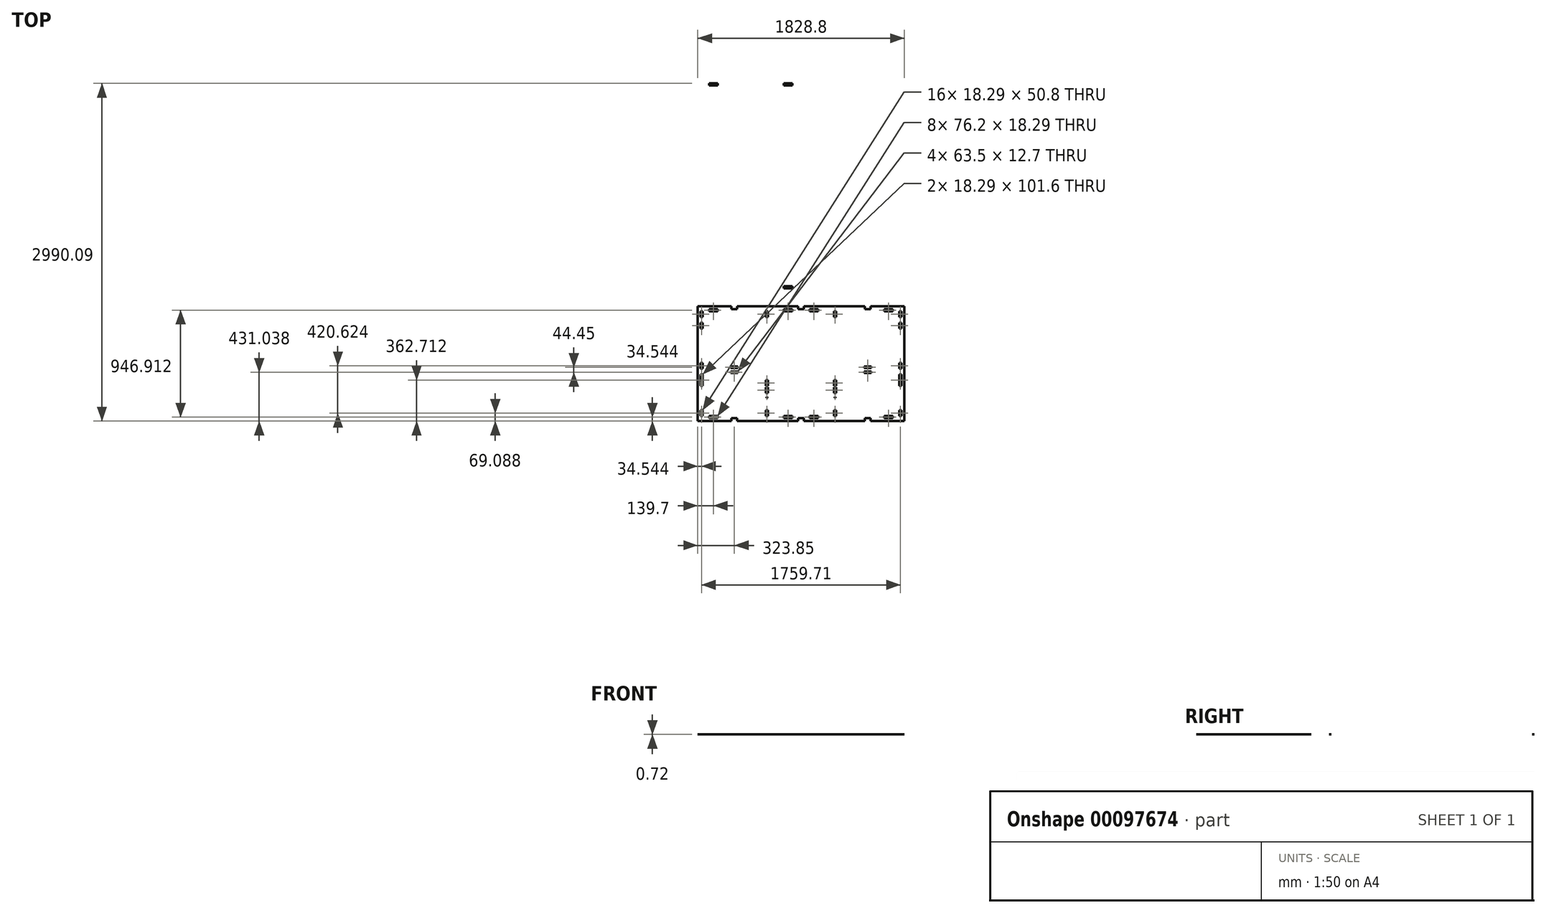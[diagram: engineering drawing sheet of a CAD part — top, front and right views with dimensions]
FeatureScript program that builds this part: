
annotation { "Feature Type Name" : "Feature", "Feature Type Description" : "" }
export const myFeature = defineFeature(function(context is Context, id is Id, definition is map)
    precondition{}
    {
        {
            assignVariable(context, id + "F0", {"name" : "ply34", "anyValue" : .72});
        }
        {
            var Q0;
            Q0=qCreatedBy(makeId("Top.planeOp"),FACE);
            var sketch = newSketch(context, id + "F1", { "sketchPlane" : qUnion([Q0])});
            skLineSegment(sketch, "E0.bottom", {"start": v(914.4, 508) * mm, "end": v(-914.4, 508) * mm});
            skLineSegment(sketch, "E0.top", {"start": v(914.4, -508) * mm, "end": v(-914.4, -508) * mm});
            skLineSegment(sketch, "E0.left", {"start": v(914.4, 508) * mm, "end": v(914.4, -508) * mm});
            skLineSegment(sketch, "E0.right", {"start": v(-914.4, 508) * mm, "end": v(-914.4, -508) * mm});
            skPoint(sketch, "E0.middle", {"position": v(0, 0) * mm});
            skLineSegment(sketch, "E1.bottom", {"start": v(889, 482.6) * mm, "end": v(-889, 482.6) * mm, "construction": true});
            skLineSegment(sketch, "E1.top", {"start": v(889, -482.6) * mm, "end": v(-889, -482.6) * mm, "construction": true});
            skLineSegment(sketch, "E1.left", {"start": v(889, 482.6) * mm, "end": v(889, -482.6) * mm, "construction": true});
            skLineSegment(sketch, "E1.right", {"start": v(-889, 482.6) * mm, "end": v(-889, -482.6) * mm, "construction": true});
            skLineSegment(sketch, "E2", {"start": v(0, 482.6) * mm, "end": v(0, -482.6) * mm, "construction": true});
            skLineSegment(sketch, "E3", {"start": v(0, 0) * mm, "end": v(-889, 0) * mm, "construction": true});
            skLineSegment(sketch, "E4", {"start": v(-444.5, 482.6) * mm, "end": v(-444.5, -482.6) * mm, "construction": true});
            skPoint(sketch, "E4.startSnap0", {"position": v(-444.5, 0) * mm});
            skLineSegment(sketch, "E5.bottom", {"start": v(-812.8, 482.6) * mm, "end": v(-736.6, 482.6) * mm});
            skLineSegment(sketch, "E5.top", {"start": v(-812.8, 464.31) * mm, "end": v(-736.6, 464.31) * mm});
            skLineSegment(sketch, "E5.left", {"start": v(-812.8, 482.6) * mm, "end": v(-812.8, 464.31) * mm});
            skLineSegment(sketch, "E5.right", {"start": v(-736.6, 482.6) * mm, "end": v(-736.6, 464.31) * mm});
            skLineSegment(sketch, "E6.MirrorCS", {"start": v(-76.2, 482.6) * mm, "end": v(-152.4, 482.6) * mm});
            skLineSegment(sketch, "E7.MirrorCS", {"start": v(-76.2, 464.31) * mm, "end": v(-152.4, 464.31) * mm});
            skLineSegment(sketch, "E8.MirrorCS", {"start": v(-152.4, 482.6) * mm, "end": v(-152.4, 464.31) * mm});
            skLineSegment(sketch, "E9.MirrorCS", {"start": v(-76.2, 482.6) * mm, "end": v(-76.2, 464.31) * mm});
            skLineSegment(sketch, "E10.MirrorCS", {"start": v(76.2, 482.6) * mm, "end": v(76.2, 464.31) * mm});
            skLineSegment(sketch, "E11.MirrorCS", {"start": v(736.6, 482.6) * mm, "end": v(736.6, 464.31) * mm});
            skLineSegment(sketch, "E12.MirrorCS", {"start": v(152.4, 482.6) * mm, "end": v(152.4, 464.31) * mm});
            skLineSegment(sketch, "E13.MirrorCS", {"start": v(812.8, 482.6) * mm, "end": v(812.8, 464.31) * mm});
            skLineSegment(sketch, "E14.MirrorCS", {"start": v(812.8, 482.6) * mm, "end": v(736.6, 482.6) * mm});
            skLineSegment(sketch, "E15.MirrorCS", {"start": v(76.2, 482.6) * mm, "end": v(152.4, 482.6) * mm});
            skLineSegment(sketch, "E16.MirrorCS", {"start": v(812.8, 464.31) * mm, "end": v(736.6, 464.31) * mm});
            skLineSegment(sketch, "E17.MirrorCS", {"start": v(76.2, 464.31) * mm, "end": v(152.4, 464.31) * mm});
            skLineSegment(sketch, "E18.MirrorCS", {"start": v(812.8, -482.6) * mm, "end": v(812.8, -464.31) * mm});
            skLineSegment(sketch, "E19.MirrorCS", {"start": v(-76.2, -482.6) * mm, "end": v(-76.2, -464.31) * mm});
            skLineSegment(sketch, "E20.MirrorCS", {"start": v(736.6, -482.6) * mm, "end": v(736.6, -464.31) * mm});
            skLineSegment(sketch, "E21.MirrorCS", {"start": v(-152.4, -482.6) * mm, "end": v(-152.4, -464.31) * mm});
            skLineSegment(sketch, "E22.MirrorCS", {"start": v(152.4, -482.6) * mm, "end": v(152.4, -464.31) * mm});
            skLineSegment(sketch, "E23.MirrorCS", {"start": v(-812.8, -482.6) * mm, "end": v(-812.8, -464.31) * mm});
            skLineSegment(sketch, "E24.MirrorCS", {"start": v(76.2, -482.6) * mm, "end": v(76.2, -464.31) * mm});
            skLineSegment(sketch, "E25.MirrorCS", {"start": v(-736.6, -482.6) * mm, "end": v(-736.6, -464.31) * mm});
            skLineSegment(sketch, "E26.MirrorCS", {"start": v(76.2, -482.6) * mm, "end": v(152.4, -482.6) * mm});
            skLineSegment(sketch, "E27.MirrorCS", {"start": v(812.8, -464.31) * mm, "end": v(736.6, -464.31) * mm});
            skLineSegment(sketch, "E28.MirrorCS", {"start": v(812.8, -482.6) * mm, "end": v(736.6, -482.6) * mm});
            skLineSegment(sketch, "E29.MirrorCS", {"start": v(-76.2, -464.31) * mm, "end": v(-152.4, -464.31) * mm});
            skLineSegment(sketch, "E30.MirrorCS", {"start": v(-76.2, -482.6) * mm, "end": v(-152.4, -482.6) * mm});
            skLineSegment(sketch, "E31.MirrorCS", {"start": v(76.2, -464.31) * mm, "end": v(152.4, -464.31) * mm});
            skLineSegment(sketch, "E32.MirrorCS", {"start": v(-812.8, -464.31) * mm, "end": v(-736.6, -464.31) * mm});
            skLineSegment(sketch, "E33.MirrorCS", {"start": v(-812.8, -482.6) * mm, "end": v(-736.6, -482.6) * mm});
            skLineSegment(sketch, "E34.bottom", {"start": v(292.1, 464.31) * mm, "end": v(310.39, 464.31) * mm});
            skLineSegment(sketch, "E34.top", {"start": v(292.1, 413.51) * mm, "end": v(310.39, 413.51) * mm});
            skLineSegment(sketch, "E34.left", {"start": v(292.1, 464.31) * mm, "end": v(292.1, 413.51) * mm});
            skLineSegment(sketch, "E34.right", {"start": v(310.39, 464.31) * mm, "end": v(310.39, 413.51) * mm});
            skLineSegment(sketch, "E35.bottom", {"start": v(292.1, -145.29) * mm, "end": v(310.39, -145.29) * mm});
            skLineSegment(sketch, "E35.top", {"start": v(292.1, -196.09) * mm, "end": v(310.39, -196.09) * mm});
            skLineSegment(sketch, "E35.left", {"start": v(292.1, -145.29) * mm, "end": v(292.1, -196.09) * mm});
            skLineSegment(sketch, "E35.right", {"start": v(310.39, -145.29) * mm, "end": v(310.39, -196.09) * mm});
            skLineSegment(sketch, "E36.MirrorCS", {"start": v(-292.1, -196.09) * mm, "end": v(-310.39, -196.09) * mm});
            skLineSegment(sketch, "E37.MirrorCS", {"start": v(-292.1, -145.29) * mm, "end": v(-310.39, -145.29) * mm});
            skLineSegment(sketch, "E38.MirrorCS", {"start": v(-292.1, 413.51) * mm, "end": v(-310.39, 413.51) * mm});
            skLineSegment(sketch, "E39.MirrorCS", {"start": v(-292.1, 464.31) * mm, "end": v(-310.39, 464.31) * mm});
            skLineSegment(sketch, "E40.MirrorCS", {"start": v(-292.1, -145.29) * mm, "end": v(-292.1, -196.09) * mm});
            skLineSegment(sketch, "E41.MirrorCS", {"start": v(-310.39, 464.31) * mm, "end": v(-310.39, 413.51) * mm});
            skLineSegment(sketch, "E42.MirrorCS", {"start": v(-310.39, -145.29) * mm, "end": v(-310.39, -196.09) * mm});
            skLineSegment(sketch, "E43.MirrorCS", {"start": v(-292.1, 464.31) * mm, "end": v(-292.1, 413.51) * mm});
            skLineSegment(sketch, "E44.bottom", {"start": v(-889, 685.8) * mm, "end": v(0, 685.8) * mm});
            skLineSegment(sketch, "E44.top", {"start": v(-889, 2463.8) * mm, "end": v(0, 2463.8) * mm});
            skLineSegment(sketch, "E44.left", {"start": v(-889, 685.8) * mm, "end": v(-889, 2463.8) * mm});
            skLineSegment(sketch, "E44.right", {"start": v(0, 685.8) * mm, "end": v(0, 2463.8) * mm});
            skLineSegment(sketch, "E45.bottom", {"start": v(-812.8, 685.8) * mm, "end": v(-736.6, 685.8) * mm});
            skLineSegment(sketch, "E45.top", {"start": v(-812.8, 667.51) * mm, "end": v(-736.6, 667.51) * mm});
            skLineSegment(sketch, "E45.left", {"start": v(-812.8, 685.8) * mm, "end": v(-812.8, 667.51) * mm});
            skLineSegment(sketch, "E45.right", {"start": v(-736.6, 685.8) * mm, "end": v(-736.6, 667.51) * mm});
            skLineSegment(sketch, "E46", {"start": v(-444.5, 685.8) * mm, "end": v(-444.5, 2463.8) * mm, "construction": true});
            skLineSegment(sketch, "E47", {"start": v(0, 1574.8) * mm, "end": v(-889, 1574.8) * mm, "construction": true});
            skLineSegment(sketch, "E48.MirrorCS", {"start": v(-76.2, 667.51) * mm, "end": v(-152.4, 667.51) * mm});
            skLineSegment(sketch, "E49.MirrorCS", {"start": v(-76.2, 685.8) * mm, "end": v(-152.4, 685.8) * mm});
            skLineSegment(sketch, "E50.MirrorCS", {"start": v(-152.4, 685.8) * mm, "end": v(-152.4, 667.51) * mm});
            skLineSegment(sketch, "E51.MirrorCS", {"start": v(-76.2, 685.8) * mm, "end": v(-76.2, 667.51) * mm});
            skLineSegment(sketch, "E52.MirrorCS", {"start": v(-812.8, 2482.09) * mm, "end": v(-736.6, 2482.09) * mm});
            skLineSegment(sketch, "E53.MirrorCS", {"start": v(-812.8, 2463.8) * mm, "end": v(-736.6, 2463.8) * mm});
            skLineSegment(sketch, "E54.MirrorCS", {"start": v(-812.8, 2463.8) * mm, "end": v(-812.8, 2482.09) * mm});
            skLineSegment(sketch, "E55.MirrorCS", {"start": v(-736.6, 2463.8) * mm, "end": v(-736.6, 2482.09) * mm});
            skLineSegment(sketch, "E56.MirrorCS", {"start": v(-152.4, 2463.8) * mm, "end": v(-152.4, 2482.09) * mm});
            skLineSegment(sketch, "E57.MirrorCS", {"start": v(-76.2, 2463.8) * mm, "end": v(-76.2, 2482.09) * mm});
            skLineSegment(sketch, "E58.MirrorCS", {"start": v(-76.2, 2482.09) * mm, "end": v(-152.4, 2482.09) * mm});
            skLineSegment(sketch, "E59.MirrorCS", {"start": v(-76.2, 2463.8) * mm, "end": v(-152.4, 2463.8) * mm});
            skLineSegment(sketch, "E60.0", {"start": v(870.71, 464.31) * mm, "end": v(-870.71, 464.31) * mm, "construction": true});
            skLineSegment(sketch, "E60.1", {"start": v(870.71, 464.31) * mm, "end": v(870.71, -464.31) * mm, "construction": true});
            skLineSegment(sketch, "E60.2", {"start": v(870.71, -464.31) * mm, "end": v(-870.71, -464.31) * mm, "construction": true});
            skLineSegment(sketch, "E60.3", {"start": v(-870.71, 464.31) * mm, "end": v(-870.71, -464.31) * mm, "construction": true});
            skLineSegment(sketch, "E61.bottom", {"start": v(-310.39, 464.31) * mm, "end": v(-292.1, 464.31) * mm, "construction": true});
            skLineSegment(sketch, "E61.top", {"start": v(-310.39, -196.09) * mm, "end": v(-292.1, -196.09) * mm, "construction": true});
            skLineSegment(sketch, "E61.left", {"start": v(-310.39, 464.31) * mm, "end": v(-310.39, -196.09) * mm, "construction": true});
            skLineSegment(sketch, "E61.right", {"start": v(-292.1, 464.31) * mm, "end": v(-292.1, -196.09) * mm, "construction": true});
            skLineSegment(sketch, "E62.bottom", {"start": v(292.1, 464.31) * mm, "end": v(310.39, 464.31) * mm, "construction": true});
            skLineSegment(sketch, "E62.top", {"start": v(292.1, -196.09) * mm, "end": v(310.39, -196.09) * mm, "construction": true});
            skLineSegment(sketch, "E62.left", {"start": v(292.1, 464.31) * mm, "end": v(292.1, -196.09) * mm, "construction": true});
            skLineSegment(sketch, "E62.right", {"start": v(310.39, 464.31) * mm, "end": v(310.39, -196.09) * mm, "construction": true});
            skLineSegment(sketch, "E63.bottom", {"start": v(889, 464.31) * mm, "end": v(870.71, 464.31) * mm});
            skLineSegment(sketch, "E63.top", {"start": v(889, 413.51) * mm, "end": v(870.71, 413.51) * mm});
            skLineSegment(sketch, "E63.left", {"start": v(889, 464.31) * mm, "end": v(889, 413.51) * mm});
            skLineSegment(sketch, "E63.right", {"start": v(870.71, 464.31) * mm, "end": v(870.71, 413.51) * mm});
            skLineSegment(sketch, "E64.bottom", {"start": v(889, -94.49) * mm, "end": v(870.71, -94.49) * mm});
            skLineSegment(sketch, "E64.top", {"start": v(889, -145.29) * mm, "end": v(870.71, -145.29) * mm});
            skLineSegment(sketch, "E64.left", {"start": v(889, -94.49) * mm, "end": v(889, -145.29) * mm});
            skLineSegment(sketch, "E64.right", {"start": v(870.71, -94.49) * mm, "end": v(870.71, -145.29) * mm});
            skLineSegment(sketch, "E65.MirrorCS", {"start": v(-889, 464.31) * mm, "end": v(-870.71, 464.31) * mm});
            skLineSegment(sketch, "E66.MirrorCS", {"start": v(-889, -145.29) * mm, "end": v(-870.71, -145.29) * mm});
            skLineSegment(sketch, "E67.MirrorCS", {"start": v(-889, -94.49) * mm, "end": v(-870.71, -94.49) * mm});
            skLineSegment(sketch, "E68.MirrorCS", {"start": v(-889, 413.51) * mm, "end": v(-870.71, 413.51) * mm});
            skLineSegment(sketch, "E69.MirrorCS", {"start": v(-870.71, -94.49) * mm, "end": v(-870.71, -145.29) * mm});
            skLineSegment(sketch, "E70.MirrorCS", {"start": v(-889, -94.49) * mm, "end": v(-889, -145.29) * mm});
            skLineSegment(sketch, "E71.MirrorCS", {"start": v(-870.71, 464.31) * mm, "end": v(-870.71, 413.51) * mm});
            skLineSegment(sketch, "E72.MirrorCS", {"start": v(-889, 464.31) * mm, "end": v(-889, 413.51) * mm});
            skLineSegment(sketch, "E73", {"start": v(-50.8, 2463.8) * mm, "end": v(-50.8, 685.8) * mm, "construction": true});
            skLineSegment(sketch, "E74.bottom", {"start": v(889, 7.11) * mm, "end": v(870.71, 7.11) * mm});
            skLineSegment(sketch, "E74.top", {"start": v(889, -43.69) * mm, "end": v(870.71, -43.69) * mm});
            skLineSegment(sketch, "E74.left", {"start": v(889, 7.11) * mm, "end": v(889, -43.69) * mm});
            skLineSegment(sketch, "E74.right", {"start": v(870.71, 7.11) * mm, "end": v(870.71, -43.69) * mm});
            skLineSegment(sketch, "E75.MirrorCS", {"start": v(-870.71, 7.11) * mm, "end": v(-870.71, -43.69) * mm});
            skLineSegment(sketch, "E76.MirrorCS", {"start": v(-889, 7.11) * mm, "end": v(-889, -43.69) * mm});
            skLineSegment(sketch, "E77.MirrorCS", {"start": v(-889, -43.69) * mm, "end": v(-870.71, -43.69) * mm});
            skLineSegment(sketch, "E78.MirrorCS", {"start": v(-889, 7.11) * mm, "end": v(-870.71, 7.11) * mm});
            skLineSegment(sketch, "E79.MirrorCS", {"start": v(-838.2, 2463.8) * mm, "end": v(-838.2, 685.8) * mm, "construction": true});
            skLineSegment(sketch, "E80.bottom", {"start": v(-50.8, 1676.4) * mm, "end": v(-69.09, 1676.4) * mm});
            skLineSegment(sketch, "E80.top", {"start": v(-50.8, 1473.2) * mm, "end": v(-69.09, 1473.2) * mm});
            skLineSegment(sketch, "E80.left", {"start": v(-50.8, 1676.4) * mm, "end": v(-50.8, 1473.2) * mm});
            skLineSegment(sketch, "E80.right", {"start": v(-69.09, 1676.4) * mm, "end": v(-69.09, 1473.2) * mm});
            skPoint(sketch, "E80.middle", {"position": v(-59.94, 1574.8) * mm});
            skLineSegment(sketch, "E81.bottom", {"start": v(-838.2, 685.8) * mm, "end": v(-819.91, 685.8) * mm});
            skLineSegment(sketch, "E81.top", {"start": v(-838.2, 698.5) * mm, "end": v(-819.91, 698.5) * mm});
            skLineSegment(sketch, "E81.left", {"start": v(-838.2, 685.8) * mm, "end": v(-838.2, 698.5) * mm});
            skLineSegment(sketch, "E81.right", {"start": v(-819.91, 685.8) * mm, "end": v(-819.91, 698.5) * mm});
            skLineSegment(sketch, "E82.MirrorCS", {"start": v(-69.09, 685.8) * mm, "end": v(-69.09, 698.5) * mm});
            skLineSegment(sketch, "E83.MirrorCS", {"start": v(-50.8, 685.8) * mm, "end": v(-50.8, 698.5) * mm});
            skLineSegment(sketch, "E84.MirrorCS", {"start": v(-50.8, 685.8) * mm, "end": v(-69.09, 685.8) * mm});
            skLineSegment(sketch, "E85.MirrorCS", {"start": v(-50.8, 698.5) * mm, "end": v(-69.09, 698.5) * mm});
            skLineSegment(sketch, "E86.MirrorCS", {"start": v(-69.09, 2463.8) * mm, "end": v(-69.09, 2451.1) * mm});
            skLineSegment(sketch, "E87.MirrorCS", {"start": v(-50.8, 2463.8) * mm, "end": v(-50.8, 2451.1) * mm});
            skLineSegment(sketch, "E88.MirrorCS", {"start": v(-50.8, 2463.8) * mm, "end": v(-69.09, 2463.8) * mm});
            skLineSegment(sketch, "E89.MirrorCS", {"start": v(-50.8, 2451.1) * mm, "end": v(-69.09, 2451.1) * mm});
            skLineSegment(sketch, "E90.MirrorCS", {"start": v(-838.2, 2463.8) * mm, "end": v(-819.91, 2463.8) * mm});
            skLineSegment(sketch, "E91.MirrorCS", {"start": v(-838.2, 2451.1) * mm, "end": v(-819.91, 2451.1) * mm});
            skLineSegment(sketch, "E92.MirrorCS", {"start": v(-819.91, 2463.8) * mm, "end": v(-819.91, 2451.1) * mm});
            skLineSegment(sketch, "E93.MirrorCS", {"start": v(-838.2, 2463.8) * mm, "end": v(-838.2, 2451.1) * mm});
            skLineSegment(sketch, "E94", {"start": v(-889, 2270.7) * mm, "end": v(0, 2270.7) * mm, "construction": true});
            skLineSegment(sketch, "E95.bottom", {"start": v(-50.8, 2359.6) * mm, "end": v(-69.09, 2359.6) * mm});
            skLineSegment(sketch, "E95.top", {"start": v(-50.8, 2181.8) * mm, "end": v(-69.09, 2181.8) * mm});
            skLineSegment(sketch, "E95.left", {"start": v(-50.8, 2359.6) * mm, "end": v(-50.8, 2181.8) * mm});
            skLineSegment(sketch, "E95.right", {"start": v(-69.09, 2359.6) * mm, "end": v(-69.09, 2181.8) * mm});
            skPoint(sketch, "E95.middle", {"position": v(-59.94, 2270.7) * mm});
            skLineSegment(sketch, "E96.MirrorCS", {"start": v(-838.2, 2181.8) * mm, "end": v(-819.91, 2181.8) * mm});
            skLineSegment(sketch, "E97.MirrorCS", {"start": v(-838.2, 2359.6) * mm, "end": v(-819.91, 2359.6) * mm});
            skLineSegment(sketch, "E98.MirrorCS", {"start": v(-819.91, 2359.6) * mm, "end": v(-819.91, 2181.8) * mm});
            skLineSegment(sketch, "E99.MirrorCS", {"start": v(-838.2, 2359.6) * mm, "end": v(-838.2, 2181.8) * mm});
            skPoint(sketch, "E100.MirrorP", {"position": v(-829.06, 2270.7) * mm});
            skLineSegment(sketch, "E101.MirrorCS", {"start": v(-50.8, 790) * mm, "end": v(-69.09, 790) * mm});
            skLineSegment(sketch, "E102.MirrorCS", {"start": v(-838.2, 967.8) * mm, "end": v(-819.91, 967.8) * mm});
            skLineSegment(sketch, "E103.MirrorCS", {"start": v(-838.2, 790) * mm, "end": v(-819.91, 790) * mm});
            skLineSegment(sketch, "E104.MirrorCS", {"start": v(-50.8, 967.8) * mm, "end": v(-69.09, 967.8) * mm});
            skLineSegment(sketch, "E105.MirrorCS", {"start": v(-50.8, 790) * mm, "end": v(-50.8, 967.8) * mm});
            skLineSegment(sketch, "E106.MirrorCS", {"start": v(-69.09, 790) * mm, "end": v(-69.09, 967.8) * mm});
            skLineSegment(sketch, "E107.MirrorCS", {"start": v(-819.91, 790) * mm, "end": v(-819.91, 967.8) * mm});
            skLineSegment(sketch, "E108.MirrorCS", {"start": v(-838.2, 790) * mm, "end": v(-838.2, 967.8) * mm});
            skPoint(sketch, "E109.MirrorP", {"position": v(-59.94, 878.9) * mm});
            skPoint(sketch, "E110.MirrorP", {"position": v(-829.06, 878.9) * mm});
            skLineSegment(sketch, "E111.MirrorCS", {"start": v(-838.2, 1473.2) * mm, "end": v(-819.91, 1473.2) * mm});
            skLineSegment(sketch, "E112.MirrorCS", {"start": v(-838.2, 1676.4) * mm, "end": v(-819.91, 1676.4) * mm});
            skPoint(sketch, "E113.MirrorP", {"position": v(-829.06, 1574.8) * mm});
            skLineSegment(sketch, "E114.MirrorCS", {"start": v(-819.91, 1676.4) * mm, "end": v(-819.91, 1473.2) * mm});
            skLineSegment(sketch, "E115.MirrorCS", {"start": v(-838.2, 1676.4) * mm, "end": v(-838.2, 1473.2) * mm});
            skLineSegment(sketch, "E116", {"start": v(-444.5, 1574.8) * mm, "end": v(-69.09, 1574.8) * mm, "construction": true});
            skLineSegment(sketch, "E117.bottom", {"start": v(870.71, -464.31) * mm, "end": v(889, -464.31) * mm});
            skLineSegment(sketch, "E117.top", {"start": v(870.71, -413.51) * mm, "end": v(889, -413.51) * mm});
            skLineSegment(sketch, "E117.left", {"start": v(870.71, -464.31) * mm, "end": v(870.71, -413.51) * mm});
            skLineSegment(sketch, "E117.right", {"start": v(889, -464.31) * mm, "end": v(889, -413.51) * mm});
            skLineSegment(sketch, "E118.bottom", {"start": v(870.71, -145.29) * mm, "end": v(889, -145.29) * mm});
            skLineSegment(sketch, "E118.top", {"start": v(870.71, -196.09) * mm, "end": v(889, -196.09) * mm});
            skLineSegment(sketch, "E118.left", {"start": v(870.71, -145.29) * mm, "end": v(870.71, -196.09) * mm});
            skLineSegment(sketch, "E118.right", {"start": v(889, -145.29) * mm, "end": v(889, -196.09) * mm});
            skLineSegment(sketch, "E119.MirrorCS", {"start": v(-889, -145.29) * mm, "end": v(-889, -196.09) * mm});
            skLineSegment(sketch, "E120.MirrorCS", {"start": v(-870.71, -145.29) * mm, "end": v(-870.71, -196.09) * mm});
            skLineSegment(sketch, "E121.MirrorCS", {"start": v(-870.71, -196.09) * mm, "end": v(-889, -196.09) * mm});
            skLineSegment(sketch, "E122.MirrorCS", {"start": v(-870.71, -464.31) * mm, "end": v(-889, -464.31) * mm});
            skLineSegment(sketch, "E123.MirrorCS", {"start": v(-889, -464.31) * mm, "end": v(-889, -413.51) * mm});
            skLineSegment(sketch, "E124.MirrorCS", {"start": v(-870.71, -464.31) * mm, "end": v(-870.71, -413.51) * mm});
            skLineSegment(sketch, "E125.MirrorCS", {"start": v(-870.71, -413.51) * mm, "end": v(-889, -413.51) * mm});
            skLineSegment(sketch, "E126.bottom", {"start": v(-889, 879.28) * mm, "end": v(-870.71, 879.28) * mm});
            skLineSegment(sketch, "E126.top", {"start": v(-889, 764.98) * mm, "end": v(-870.71, 764.98) * mm});
            skLineSegment(sketch, "E126.left", {"start": v(-889, 879.28) * mm, "end": v(-889, 764.98) * mm});
            skLineSegment(sketch, "E126.right", {"start": v(-870.71, 879.28) * mm, "end": v(-870.71, 764.98) * mm});
            skPoint(sketch, "E126.middle", {"position": v(-879.86, 822.13) * mm});
            skLineSegment(sketch, "E127.bottom", {"start": v(-889, 1428.75) * mm, "end": v(-870.71, 1428.75) * mm});
            skLineSegment(sketch, "E127.top", {"start": v(-889, 1543.05) * mm, "end": v(-870.71, 1543.05) * mm});
            skLineSegment(sketch, "E127.left", {"start": v(-889, 1428.75) * mm, "end": v(-889, 1543.05) * mm});
            skLineSegment(sketch, "E127.right", {"start": v(-870.71, 1428.75) * mm, "end": v(-870.71, 1543.05) * mm});
            skPoint(sketch, "E127.middle", {"position": v(-879.86, 1485.9) * mm});
            skLineSegment(sketch, "E128", {"start": v(-879.86, 822.13) * mm, "end": v(-879.86, 685.8) * mm, "construction": true});
            skLineSegment(sketch, "E129", {"start": v(-879.86, 1485.9) * mm, "end": v(-879.86, 685.8) * mm, "construction": true});
            skLineSegment(sketch, "E130.MirrorCS", {"start": v(0, 879.28) * mm, "end": v(-18.29, 879.28) * mm});
            skLineSegment(sketch, "E131.MirrorCS", {"start": v(0, 879.28) * mm, "end": v(0, 764.98) * mm});
            skLineSegment(sketch, "E132.MirrorCS", {"start": v(-18.29, 1428.75) * mm, "end": v(-18.29, 1543.05) * mm});
            skPoint(sketch, "E133.MirrorP", {"position": v(-9.14, 1485.9) * mm});
            skLineSegment(sketch, "E134.MirrorCS", {"start": v(0, 1428.75) * mm, "end": v(0, 1543.05) * mm});
            skPoint(sketch, "E135.MirrorP", {"position": v(-9.14, 822.13) * mm});
            skLineSegment(sketch, "E136.MirrorCS", {"start": v(0, 1543.05) * mm, "end": v(-18.29, 1543.05) * mm});
            skLineSegment(sketch, "E137.MirrorCS", {"start": v(0, 764.98) * mm, "end": v(-18.29, 764.98) * mm});
            skLineSegment(sketch, "E138.MirrorCS", {"start": v(0, 1428.75) * mm, "end": v(-18.29, 1428.75) * mm});
            skLineSegment(sketch, "E139.MirrorCS", {"start": v(-18.29, 879.28) * mm, "end": v(-18.29, 764.98) * mm});
            skLineSegment(sketch, "E140.MirrorCS", {"start": v(-889, 2270.32) * mm, "end": v(-870.71, 2270.32) * mm});
            skLineSegment(sketch, "E141.MirrorCS", {"start": v(-889, 2384.62) * mm, "end": v(-870.71, 2384.62) * mm});
            skLineSegment(sketch, "E142.MirrorCS", {"start": v(-889, 2270.32) * mm, "end": v(-889, 2384.62) * mm});
            skLineSegment(sketch, "E143.MirrorCS", {"start": v(-870.71, 2270.32) * mm, "end": v(-870.71, 2384.62) * mm});
            skLineSegment(sketch, "E144.MirrorCS", {"start": v(-889, 1720.85) * mm, "end": v(-870.71, 1720.85) * mm});
            skLineSegment(sketch, "E145.MirrorCS", {"start": v(-889, 1606.55) * mm, "end": v(-870.71, 1606.55) * mm});
            skPoint(sketch, "E146.MirrorP", {"position": v(-879.86, 2327.47) * mm});
            skLineSegment(sketch, "E147.MirrorCS", {"start": v(-889, 1720.85) * mm, "end": v(-889, 1606.55) * mm});
            skPoint(sketch, "E148.MirrorP", {"position": v(-879.86, 1663.7) * mm});
            skLineSegment(sketch, "E149.MirrorCS", {"start": v(-870.71, 1720.85) * mm, "end": v(-870.71, 1606.55) * mm});
            skLineSegment(sketch, "E150.MirrorCS", {"start": v(0, 1720.85) * mm, "end": v(-18.29, 1720.85) * mm});
            skLineSegment(sketch, "E151.MirrorCS", {"start": v(0, 2384.62) * mm, "end": v(-18.29, 2384.62) * mm});
            skLineSegment(sketch, "E152.MirrorCS", {"start": v(0, 2270.32) * mm, "end": v(-18.29, 2270.32) * mm});
            skLineSegment(sketch, "E153.MirrorCS", {"start": v(0, 1606.55) * mm, "end": v(-18.29, 1606.55) * mm});
            skLineSegment(sketch, "E154.MirrorCS", {"start": v(0, 1720.85) * mm, "end": v(0, 1606.55) * mm});
            skLineSegment(sketch, "E155.MirrorCS", {"start": v(-18.29, 1720.85) * mm, "end": v(-18.29, 1606.55) * mm});
            skLineSegment(sketch, "E156.MirrorCS", {"start": v(-18.29, 2270.32) * mm, "end": v(-18.29, 2384.62) * mm});
            skLineSegment(sketch, "E157.MirrorCS", {"start": v(0, 2270.32) * mm, "end": v(0, 2384.62) * mm});
            skPoint(sketch, "E158.MirrorP", {"position": v(-9.14, 2327.47) * mm});
            skPoint(sketch, "E159.MirrorP", {"position": v(-9.14, 1663.7) * mm});
            skLineSegment(sketch, "E160.0", {"start": v(-889, 692.15) * mm, "end": v(0, 692.15) * mm, "construction": true});
            skLineSegment(sketch, "E161.bottom", {"start": v(-292.1, 1098.55) * mm, "end": v(-310.39, 1098.55) * mm});
            skLineSegment(sketch, "E161.top", {"start": v(-292.1, 1212.85) * mm, "end": v(-310.39, 1212.85) * mm});
            skLineSegment(sketch, "E161.left", {"start": v(-292.1, 1098.55) * mm, "end": v(-292.1, 1212.85) * mm});
            skLineSegment(sketch, "E161.right", {"start": v(-310.39, 1098.55) * mm, "end": v(-310.39, 1212.85) * mm});
            skPoint(sketch, "E161.middle", {"position": v(-301.24, 1155.7) * mm});
            skPoint(sketch, "E161.middle.positionSnap0", {"position": v(-301.24, 464.31) * mm});
            skPoint(sketch, "E161.centerSnap0", {"position": v(-301.24, 464.31) * mm});
            skLineSegment(sketch, "E162.MirrorCS", {"start": v(-596.9, 1212.85) * mm, "end": v(-578.61, 1212.85) * mm});
            skLineSegment(sketch, "E163.MirrorCS", {"start": v(-596.9, 1098.55) * mm, "end": v(-578.61, 1098.55) * mm});
            skLineSegment(sketch, "E164.MirrorCS", {"start": v(-596.9, 1098.55) * mm, "end": v(-596.9, 1212.85) * mm});
            skLineSegment(sketch, "E165.MirrorCS", {"start": v(-578.61, 1098.55) * mm, "end": v(-578.61, 1212.85) * mm});
            skPoint(sketch, "E166.MirrorP", {"position": v(-587.76, 1155.7) * mm});
            skLineSegment(sketch, "E167.MirrorCS", {"start": v(-292.1, 2051.05) * mm, "end": v(-310.39, 2051.05) * mm});
            skLineSegment(sketch, "E168.MirrorCS", {"start": v(-292.1, 1936.75) * mm, "end": v(-310.39, 1936.75) * mm});
            skLineSegment(sketch, "E169.MirrorCS", {"start": v(-596.9, 2051.05) * mm, "end": v(-578.61, 2051.05) * mm});
            skLineSegment(sketch, "E170.MirrorCS", {"start": v(-596.9, 1936.75) * mm, "end": v(-578.61, 1936.75) * mm});
            skLineSegment(sketch, "E171.MirrorCS", {"start": v(-292.1, 2051.05) * mm, "end": v(-292.1, 1936.75) * mm});
            skLineSegment(sketch, "E172.MirrorCS", {"start": v(-596.9, 2051.05) * mm, "end": v(-596.9, 1936.75) * mm});
            skLineSegment(sketch, "E173.MirrorCS", {"start": v(-578.61, 2051.05) * mm, "end": v(-578.61, 1936.75) * mm});
            skLineSegment(sketch, "E174.MirrorCS", {"start": v(-310.39, 2051.05) * mm, "end": v(-310.39, 1936.75) * mm});
            skPoint(sketch, "E175.MirrorP", {"position": v(-301.24, 1993.9) * mm});
            skPoint(sketch, "E176.MirrorP", {"position": v(-587.76, 1993.9) * mm});
            skLineSegment(sketch, "E177", {"start": v(-310.39, 134.11) * mm, "end": v(-870.71, 134.11) * mm, "construction": true});
            skLineSegment(sketch, "E178", {"start": v(-292.1, 134.11) * mm, "end": v(292.1, 134.11) * mm, "construction": true});
            skLineSegment(sketch, "E179.bottom", {"start": v(-615.95, 508) * mm, "end": v(-565.15, 508) * mm});
            skLineSegment(sketch, "E179.top", {"start": v(-615.95, 482.6) * mm, "end": v(-565.15, 482.6) * mm});
            skLineSegment(sketch, "E179.left", {"start": v(-615.95, 508) * mm, "end": v(-615.95, 482.6) * mm});
            skLineSegment(sketch, "E179.right", {"start": v(-565.15, 508) * mm, "end": v(-565.15, 482.6) * mm});
            skPoint(sketch, "E179.middle", {"position": v(-590.55, 495.3) * mm});
            skPoint(sketch, "E179.middle.positionSnap0", {"position": v(-590.55, 134.11) * mm});
            skPoint(sketch, "E179.centerSnap0", {"position": v(-590.55, 134.11) * mm});
            skLineSegment(sketch, "E180.bottom", {"start": v(-25.4, 508) * mm, "end": v(25.4, 508) * mm});
            skLineSegment(sketch, "E180.top", {"start": v(-25.4, 482.6) * mm, "end": v(25.4, 482.6) * mm});
            skLineSegment(sketch, "E180.left", {"start": v(-25.4, 508) * mm, "end": v(-25.4, 482.6) * mm});
            skLineSegment(sketch, "E180.right", {"start": v(25.4, 508) * mm, "end": v(25.4, 482.6) * mm});
            skPoint(sketch, "E180.middle", {"position": v(0, 495.3) * mm});
            skLineSegment(sketch, "E181.MirrorCS", {"start": v(565.15, 508) * mm, "end": v(565.15, 482.6) * mm});
            skLineSegment(sketch, "E182.MirrorCS", {"start": v(615.95, 508) * mm, "end": v(615.95, 482.6) * mm});
            skLineSegment(sketch, "E183.MirrorCS", {"start": v(615.95, 482.6) * mm, "end": v(565.15, 482.6) * mm});
            skLineSegment(sketch, "E184.MirrorCS", {"start": v(615.95, 508) * mm, "end": v(565.15, 508) * mm});
            skPoint(sketch, "E185.MirrorP", {"position": v(590.55, 495.3) * mm});
            skLineSegment(sketch, "E186.MirrorCS", {"start": v(-615.95, -508) * mm, "end": v(-565.15, -508) * mm});
            skLineSegment(sketch, "E187.MirrorCS", {"start": v(-615.95, -482.6) * mm, "end": v(-565.15, -482.6) * mm});
            skLineSegment(sketch, "E188.MirrorCS", {"start": v(-615.95, -508) * mm, "end": v(-615.95, -482.6) * mm});
            skLineSegment(sketch, "E189.MirrorCS", {"start": v(-565.15, -508) * mm, "end": v(-565.15, -482.6) * mm});
            skPoint(sketch, "E190.MirrorP", {"position": v(-590.55, -495.3) * mm});
            skLineSegment(sketch, "E191.MirrorCS", {"start": v(-25.4, -508) * mm, "end": v(25.4, -508) * mm});
            skLineSegment(sketch, "E192.MirrorCS", {"start": v(-25.4, -482.6) * mm, "end": v(25.4, -482.6) * mm});
            skLineSegment(sketch, "E193.MirrorCS", {"start": v(-25.4, -508) * mm, "end": v(-25.4, -482.6) * mm});
            skPoint(sketch, "E194.MirrorP", {"position": v(0, -495.3) * mm});
            skLineSegment(sketch, "E195.MirrorCS", {"start": v(25.4, -508) * mm, "end": v(25.4, -482.6) * mm});
            skLineSegment(sketch, "E196.MirrorCS", {"start": v(615.95, -508) * mm, "end": v(565.15, -508) * mm});
            skLineSegment(sketch, "E197.MirrorCS", {"start": v(615.95, -482.6) * mm, "end": v(565.15, -482.6) * mm});
            skPoint(sketch, "E198.MirrorP", {"position": v(590.55, -495.3) * mm});
            skLineSegment(sketch, "E199.MirrorCS", {"start": v(615.95, -508) * mm, "end": v(615.95, -482.6) * mm});
            skLineSegment(sketch, "E200.MirrorCS", {"start": v(565.15, -508) * mm, "end": v(565.15, -482.6) * mm});
            skLineSegment(sketch, "E201.bottom", {"start": v(889, 362.71) * mm, "end": v(870.71, 362.71) * mm});
            skLineSegment(sketch, "E201.top", {"start": v(889, 311.91) * mm, "end": v(870.71, 311.91) * mm});
            skLineSegment(sketch, "E201.left", {"start": v(889, 362.71) * mm, "end": v(889, 311.91) * mm});
            skLineSegment(sketch, "E201.right", {"start": v(870.71, 362.71) * mm, "end": v(870.71, 311.91) * mm});
            skLineSegment(sketch, "E202.MirrorCS", {"start": v(-870.71, 362.71) * mm, "end": v(-870.71, 311.91) * mm});
            skLineSegment(sketch, "E203.MirrorCS", {"start": v(-889, 362.71) * mm, "end": v(-889, 311.91) * mm});
            skLineSegment(sketch, "E204.MirrorCS", {"start": v(-889, 311.91) * mm, "end": v(-870.71, 311.91) * mm});
            skLineSegment(sketch, "E205.MirrorCS", {"start": v(-889, 362.71) * mm, "end": v(-870.71, 362.71) * mm});
            skLineSegment(sketch, "E206.bottom", {"start": v(-736.6, 685.8) * mm, "end": v(-152.4, 685.8) * mm});
            skLineSegment(sketch, "E206.top", {"start": v(-736.6, 736.6) * mm, "end": v(-152.4, 736.6) * mm});
            skLineSegment(sketch, "E206.left", {"start": v(-736.6, 685.8) * mm, "end": v(-736.6, 736.6) * mm});
            skLineSegment(sketch, "E206.right", {"start": v(-152.4, 685.8) * mm, "end": v(-152.4, 736.6) * mm});
            skLineSegment(sketch, "E207.MirrorCS", {"start": v(-736.6, 2463.8) * mm, "end": v(-736.6, 2413) * mm});
            skLineSegment(sketch, "E208.MirrorCS", {"start": v(-736.6, 2413) * mm, "end": v(-152.4, 2413) * mm});
            skLineSegment(sketch, "E209.MirrorCS", {"start": v(-152.4, 2463.8) * mm, "end": v(-152.4, 2413) * mm});
            skCircle(sketch, "E210", {"center": v(-9.14, 1168.4) * mm, "radius": 3.81 * mm});
            skPoint(sketch, "E210.centerSnap0", {"position": v(-9.14, 879.28) * mm});
            skCircle(sketch, "E211.MirrorC", {"center": v(-879.86, 1168.4) * mm, "radius": 3.81 * mm});
            skCircle(sketch, "E212.MirrorC", {"center": v(-879.86, 1981.2) * mm, "radius": 3.81 * mm});
            skCircle(sketch, "E213.MirrorC", {"center": v(-9.14, 1981.2) * mm, "radius": 3.81 * mm});
            skLineSegment(sketch, "E214", {"start": v(-444.5, 768.35) * mm, "end": v(-495.3, 768.35) * mm});
            skLineSegment(sketch, "E215", {"start": v(-444.5, 768.35) * mm, "end": v(-393.7, 768.35) * mm});
            skLineSegment(sketch, "E216.bottom", {"start": v(-495.3, 768.35) * mm, "end": v(-393.7, 768.35) * mm});
            skLineSegment(sketch, "E216.top", {"start": v(-495.3, 781.05) * mm, "end": v(-393.7, 781.05) * mm});
            skLineSegment(sketch, "E216.left", {"start": v(-495.3, 768.35) * mm, "end": v(-495.3, 781.05) * mm});
            skLineSegment(sketch, "E216.right", {"start": v(-393.7, 768.35) * mm, "end": v(-393.7, 781.05) * mm});
            skLineSegment(sketch, "E217.MirrorCS", {"start": v(-393.7, 2381.25) * mm, "end": v(-393.7, 2368.55) * mm});
            skLineSegment(sketch, "E218.MirrorCS", {"start": v(-495.3, 2381.25) * mm, "end": v(-495.3, 2368.55) * mm});
            skLineSegment(sketch, "E219.MirrorCS", {"start": v(-444.5, 2381.25) * mm, "end": v(-393.7, 2381.25) * mm});
            skLineSegment(sketch, "E220.MirrorCS", {"start": v(-444.5, 2381.25) * mm, "end": v(-495.3, 2381.25) * mm});
            skLineSegment(sketch, "E221.MirrorCS", {"start": v(-495.3, 2368.55) * mm, "end": v(-393.7, 2368.55) * mm});
            skLineSegment(sketch, "E222.MirrorCS", {"start": v(-495.3, 2381.25) * mm, "end": v(-393.7, 2381.25) * mm});
            skLineSegment(sketch, "E223", {"start": v(736.6, -464.31) * mm, "end": v(736.6, -83.31) * mm, "construction": true});
            skLineSegment(sketch, "E224.bottom", {"start": v(622.3, -83.31) * mm, "end": v(558.8, -83.31) * mm});
            skLineSegment(sketch, "E224.top", {"start": v(622.3, -70.61) * mm, "end": v(558.8, -70.61) * mm});
            skLineSegment(sketch, "E224.left", {"start": v(622.3, -83.31) * mm, "end": v(622.3, -70.61) * mm});
            skLineSegment(sketch, "E224.right", {"start": v(558.8, -83.31) * mm, "end": v(558.8, -70.61) * mm});
            skPoint(sketch, "E224.middle", {"position": v(590.55, -76.96) * mm});
            skLineSegment(sketch, "E225.bottom", {"start": v(622.3, -38.86) * mm, "end": v(558.8, -38.86) * mm});
            skLineSegment(sketch, "E225.top", {"start": v(622.3, -26.16) * mm, "end": v(558.8, -26.16) * mm});
            skLineSegment(sketch, "E225.left", {"start": v(622.3, -38.86) * mm, "end": v(622.3, -26.16) * mm});
            skLineSegment(sketch, "E225.right", {"start": v(558.8, -38.86) * mm, "end": v(558.8, -26.16) * mm});
            skPoint(sketch, "E225.middle", {"position": v(590.55, -32.51) * mm});
            skLineSegment(sketch, "E226.MirrorCS", {"start": v(-558.8, -38.86) * mm, "end": v(-558.8, -26.16) * mm});
            skLineSegment(sketch, "E227.MirrorCS", {"start": v(-622.3, -38.86) * mm, "end": v(-622.3, -26.16) * mm});
            skLineSegment(sketch, "E228.MirrorCS", {"start": v(-558.8, -83.31) * mm, "end": v(-558.8, -70.61) * mm});
            skLineSegment(sketch, "E229.MirrorCS", {"start": v(-622.3, -83.31) * mm, "end": v(-622.3, -70.61) * mm});
            skPoint(sketch, "E230.MirrorP", {"position": v(-590.55, -32.51) * mm});
            skLineSegment(sketch, "E231.MirrorCS", {"start": v(-622.3, -26.16) * mm, "end": v(-558.8, -26.16) * mm});
            skLineSegment(sketch, "E232.MirrorCS", {"start": v(-622.3, -38.86) * mm, "end": v(-558.8, -38.86) * mm});
            skPoint(sketch, "E233.MirrorP", {"position": v(-590.55, -76.96) * mm});
            skLineSegment(sketch, "E234.MirrorCS", {"start": v(-622.3, -83.31) * mm, "end": v(-558.8, -83.31) * mm});
            skLineSegment(sketch, "E235.MirrorCS", {"start": v(-622.3, -70.61) * mm, "end": v(-558.8, -70.61) * mm});
            skPoint(sketch, "E236.MirrorP", {"position": v(-301.24, -464.31) * mm});
            skLineSegment(sketch, "E237.MirrorCS", {"start": v(-310.39, -464.31) * mm, "end": v(-292.1, -464.31) * mm, "construction": true});
            skLineSegment(sketch, "E238.MirrorCS", {"start": v(-292.1, -464.31) * mm, "end": v(-292.1, -413.51) * mm});
            skLineSegment(sketch, "E239.MirrorCS", {"start": v(-310.39, -464.31) * mm, "end": v(-310.39, -413.51) * mm});
            skLineSegment(sketch, "E240.MirrorCS", {"start": v(-292.1, -464.31) * mm, "end": v(-310.39, -464.31) * mm});
            skLineSegment(sketch, "E241.MirrorCS", {"start": v(-292.1, -413.51) * mm, "end": v(-310.39, -413.51) * mm});
            skLineSegment(sketch, "E242.MirrorCS", {"start": v(292.1, -464.31) * mm, "end": v(310.39, -464.31) * mm, "construction": true});
            skLineSegment(sketch, "E243.MirrorCS", {"start": v(292.1, -464.31) * mm, "end": v(292.1, -413.51) * mm});
            skLineSegment(sketch, "E244.MirrorCS", {"start": v(310.39, -464.31) * mm, "end": v(310.39, -413.51) * mm});
            skLineSegment(sketch, "E245.MirrorCS", {"start": v(292.1, -464.31) * mm, "end": v(310.39, -464.31) * mm});
            skLineSegment(sketch, "E246.MirrorCS", {"start": v(292.1, -413.51) * mm, "end": v(310.39, -413.51) * mm});
            skLineSegment(sketch, "E247", {"start": v(0, -464.31) * mm, "end": v(0, -210.31) * mm, "construction": true});
            skLineSegment(sketch, "E248", {"start": v(0, -337.31) * mm, "end": v(-292.1, -337.31) * mm, "construction": true});
            skPoint(sketch, "E249.MirrorP", {"position": v(-301.24, -210.31) * mm});
            skLineSegment(sketch, "E250.MirrorCS", {"start": v(-310.39, -210.31) * mm, "end": v(-292.1, -210.31) * mm, "construction": true});
            skLineSegment(sketch, "E251.MirrorCS", {"start": v(-292.1, -261.11) * mm, "end": v(-310.39, -261.11) * mm});
            skLineSegment(sketch, "E252.MirrorCS", {"start": v(-292.1, -210.31) * mm, "end": v(-310.39, -210.31) * mm});
            skLineSegment(sketch, "E253.MirrorCS", {"start": v(-310.39, -210.31) * mm, "end": v(-310.39, -261.11) * mm});
            skLineSegment(sketch, "E254.MirrorCS", {"start": v(-292.1, -210.31) * mm, "end": v(-292.1, -261.11) * mm});
            skLineSegment(sketch, "E255.MirrorCS", {"start": v(310.39, -210.31) * mm, "end": v(292.1, -210.31) * mm, "construction": true});
            skPoint(sketch, "E256.MirrorP", {"position": v(301.24, -210.31) * mm});
            skLineSegment(sketch, "E257.MirrorCS", {"start": v(292.1, -210.31) * mm, "end": v(310.39, -210.31) * mm});
            skLineSegment(sketch, "E258.MirrorCS", {"start": v(310.39, -210.31) * mm, "end": v(310.39, -261.11) * mm});
            skLineSegment(sketch, "E259.MirrorCS", {"start": v(292.1, -210.31) * mm, "end": v(292.1, -261.11) * mm});
            skLineSegment(sketch, "E260.MirrorCS", {"start": v(292.1, -261.11) * mm, "end": v(310.39, -261.11) * mm});
            skCircle(sketch, "E261", {"center": v(301.24, -299.21) * mm, "radius": 3.81 * mm});
            skPoint(sketch, "E261.centerSnap0", {"position": v(301.24, -261.11) * mm});
            skCircle(sketch, "E262.MirrorC", {"center": v(-301.24, -299.21) * mm, "radius": 3.81 * mm});
            skCircle(sketch, "E263", {"center": v(-59.94, 1155.7) * mm, "radius": 5.59 * mm});
            skPoint(sketch, "E263.centerSnap0", {"position": v(-59.94, 1473.2) * mm});
            skPoint(sketch, "E263.centerSnap1", {"position": v(-292.1, 1155.7) * mm});
            skSolve(sketch);
        }
        {
            var Q0;
            {var subQ25=sQuery(id+"F1.wireOp",EDGE,"E45.bottom");Q0=makeQuery(id+"F1.imprint","IMPRINT",FACE,{"disambiguationData":[TD([[makeQuery(id+"F1.imprint","IMPRINT",EDGE,{"derivedFrom":subQ25}),1.0]])]});}
            var Q1;
            Q1=makeQuery(id+"F1.imprint","IMPRINT",FACE,{"disambiguationData":[TD([[makeQuery(id+"F1.imprint","IMPRINT",EDGE,{"derivedFrom":sQuery(id+"F1.wireOp",EDGE,"E52.MirrorCS")}),-1.0]])]});
            var Q2;
            Q2=makeQuery(id+"F1.imprint","IMPRINT",FACE,{"disambiguationData":[TD([[makeQuery(id+"F1.imprint","IMPRINT",EDGE,{"derivedFrom":sQuery(id+"F1.wireOp",EDGE,"E56.MirrorCS")}),-1.0]])]});
            var Q3;
            Q3=makeQuery(id+"F1.imprint","IMPRINT",FACE,{"disambiguationData":[TD([[makeQuery(id+"F1.imprint","IMPRINT",EDGE,{"derivedFrom":sQuery(id+"F1.wireOp",EDGE,"E48.MirrorCS")}),-1.0]])]});
            var Q4;
            Q4=makeQuery(id+"F1.imprint","IMPRINT",FACE,{"disambiguationData":[TD([[makeQuery(id+"F1.imprint","IMPRINT",EDGE,{"derivedFrom":sQuery(id+"F1.wireOp",EDGE,"E45.bottom")}),-1.0]])]});
            var Q5;
            Q5=makeQuery(id+"F1.imprint","IMPRINT",FACE,{"disambiguationData":[TD([[makeQuery(id+"F1.imprint","IMPRINT",EDGE,{"derivedFrom":sQuery(id+"F1.wireOp",EDGE,"lPRgTq6e-F4k6-UoHw-mTD8-ih5gjffwEfO9.bottom")}),1.0]])]});
            var Q6;
            Q6=makeQuery(id+"F1.imprint","IMPRINT",FACE,{"disambiguationData":[TD([[makeQuery(id+"F1.imprint","IMPRINT",EDGE,{"derivedFrom":sQuery(id+"F1.wireOp",EDGE,"gyY475Sn-bjW0-G2cc-n31Y-4Yqe4K2NrVFk.bottom")}),-1.0]])]});
            var Q7;
            Q7=makeQuery(id+"F1.imprint","IMPRINT",FACE,{"disambiguationData":[TD([[makeQuery(id+"F1.imprint","IMPRINT",EDGE,{"derivedFrom":sQuery(id+"F1.wireOp",EDGE,"72fbf2ea-c415-4bee-a7e0-79212a51e4920.MirrorCS")}),1.0]])]});
            var Q8;
            Q8=makeQuery(id+"F1.imprint","IMPRINT",FACE,{"disambiguationData":[TD([[makeQuery(id+"F1.imprint","IMPRINT",EDGE,{"derivedFrom":sQuery(id+"F1.wireOp",EDGE,"onFWfmD7-qhAL-YHlr-EG8H-m6XrfJa6mf9g.bottom")}),-1.0]])]});
            var Q9;
            Q9=makeQuery(id+"F1.imprint","IMPRINT",FACE,{"disambiguationData":[TD([[makeQuery(id+"F1.imprint","IMPRINT",EDGE,{"derivedFrom":sQuery(id+"F1.wireOp",EDGE,"d73ac4fc-4bd7-42c5-b921-f78bc2d6ad4e0.MirrorCS")}),-1.0]])]});
            var Q10;
            Q10=makeQuery(id+"F1.imprint","IMPRINT",FACE,{"disambiguationData":[TD([[makeQuery(id+"F1.imprint","IMPRINT",EDGE,{"derivedFrom":sQuery(id+"F1.wireOp",EDGE,"oLrFFXfg-RMGg-YdoR-4evf-nQWV7rSOX1PD.top")}),1.0]])]});
            var Q11;
            Q11=makeQuery(id+"F1.imprint","IMPRINT",FACE,{"disambiguationData":[TD([[makeQuery(id+"F1.imprint","IMPRINT",EDGE,{"derivedFrom":sQuery(id+"F1.wireOp",EDGE,"aGoaqW0x-QHaD-HELO-9l06-QiNJGT5DcYrH.bottom")}),1.0]])]});
            var Q12;
            Q12=makeQuery(id+"F1.imprint","IMPRINT",FACE,{"disambiguationData":[TD([[makeQuery(id+"F1.imprint","IMPRINT",EDGE,{"derivedFrom":sQuery(id+"F1.wireOp",EDGE,"06cf5a3d-f703-4227-b2b2-3bcf0e31aba68.MirrorCS")}),-1.0]])]});
            var Q13;
            Q13=makeQuery(id+"F1.imprint","IMPRINT",FACE,{"disambiguationData":[TD([[makeQuery(id+"F1.imprint","IMPRINT",EDGE,{"derivedFrom":sQuery(id+"F1.wireOp",EDGE,"06cf5a3d-f703-4227-b2b2-3bcf0e31aba61.MirrorCS")}),1.0]])]});
            var Q14;
            {var subQ14=sQuery(id+"F1.wireOp",EDGE,"E0.left");Q14=makeQuery(id+"F1.imprint","IMPRINT",FACE,{"disambiguationData":[TD([[makeQuery(id+"F1.imprint","IMPRINT",EDGE,{"derivedFrom":subQ14}),-1.0]])]});}
            var Q15;
            {var subQ8=sQuery(id+"F1.wireOp",EDGE,"cB0tEcp6-CMma-Govy-rMVk-1pmJY01VgE4J");Q15=makeQuery(id+"F1.imprint","IMPRINT",FACE,{"disambiguationData":[TD([[makeQuery(id+"F1.imprint","IMPRINT",EDGE,{"derivedFrom":subQ8}),-1.0]])]});}
            var Q16;
            Q16=makeQuery(id+"F1.imprint","IMPRINT",FACE,{"disambiguationData":[TD([[makeQuery(id+"F1.imprint","IMPRINT",EDGE,{"derivedFrom":sQuery(id+"F1.wireOp",EDGE,"b6b4323b-6fec-415f-982b-d5d4c1fde50a0.MirrorCS")}),-1.0]])]});
            var Q17;
            Q17=makeQuery(id+"F1.imprint","IMPRINT",FACE,{"disambiguationData":[TD([[makeQuery(id+"F1.imprint","IMPRINT",EDGE,{"derivedFrom":sQuery(id+"F1.wireOp",EDGE,"1QdwlqP9-YWuI-zVTS-cE8i-V2yDNV3nsbu3.bottom")}),1.0]])]});
            var Q18;
            Q18=makeQuery(id+"F1.imprint","IMPRINT",FACE,{"disambiguationData":[TD([[makeQuery(id+"F1.imprint","IMPRINT",EDGE,{"derivedFrom":sQuery(id+"F1.wireOp",EDGE,"tQe1WGke-olnm-fWTP-ZqGC-xnbbzDKl2nYl.bottom")}),-1.0]])]});
            var Q19;
            Q19=makeQuery(id+"F1.imprint","IMPRINT",FACE,{"disambiguationData":[TD([[makeQuery(id+"F1.imprint","IMPRINT",EDGE,{"derivedFrom":sQuery(id+"F1.wireOp",EDGE,"CCXpRIpO-Yuw9-vYaB-nys5-GNRLZybsXQPS.bottom")}),1.0]])]});
            var Q20;
            Q20=makeQuery(id+"F1.imprint","IMPRINT",FACE,{"disambiguationData":[TD([[makeQuery(id+"F1.imprint","IMPRINT",EDGE,{"derivedFrom":sQuery(id+"F1.wireOp",EDGE,"hs2pEvvn-hDQs-uA8H-EhtV-CCZwLrcSXEks.bottom")}),-1.0]])]});
            var Q21;
            Q21=makeQuery(id+"F1.imprint","IMPRINT",FACE,{"disambiguationData":[TD([[makeQuery(id+"F1.imprint","IMPRINT",EDGE,{"derivedFrom":sQuery(id+"F1.wireOp",EDGE,"iqGOsPrp-JWfh-Q1Wi-kQ2r-S8LB6Dzwkaza.top")}),-1.0]])]});
            var Q22;
            Q22=makeQuery(id+"F1.imprint","IMPRINT",FACE,{"disambiguationData":[TD([[makeQuery(id+"F1.imprint","IMPRINT",EDGE,{"derivedFrom":sQuery(id+"F1.wireOp",EDGE,"ccde4430-84ed-4c45-b490-af384d9dc54b0.MirrorCS")}),1.0]])]});
            var Q23;
            {var subQ0=sQuery(id+"F1.wireOp",EDGE,"anXlAEgO-8Pkm-WAI5-DLkZ-bVZDJHdWK94l.bottom");Q23=makeQuery(id+"F1.imprint","IMPRINT",FACE,{"disambiguationData":[TD([[makeQuery(id+"F1.imprint","IMPRINT",EDGE,{"derivedFrom":subQ0}),-1.0]])]});}
            var Q24;
            {var subQ0=sQuery(id+"F1.wireOp",EDGE,"i32ZQt6t-LSXK-j2Jt-U4Zz-f0Rd1e5JA3oz.bottom");Q24=makeQuery(id+"F1.imprint","IMPRINT",FACE,{"disambiguationData":[TD([[makeQuery(id+"F1.imprint","IMPRINT",EDGE,{"derivedFrom":subQ0}),-1.0]])]});}
            var Q25;
            {var subQ3=sQuery(id+"F1.wireOp",EDGE,"WtsgpIBi-4Pgs-vpCz-esYo-Cnh6GpizcfSd.bottom");Q25=makeQuery(id+"F1.imprint","IMPRINT",FACE,{"disambiguationData":[TD([[makeQuery(id+"F1.imprint","IMPRINT",EDGE,{"derivedFrom":subQ3}),1.0]])]});}
            var Q26;
            {var subQ0=sQuery(id+"F1.wireOp",EDGE,"yUUwdcNO-9ffT-BG9A-u9id-Sb76Se3GQj00");Q26=makeQuery(id+"F1.imprint","IMPRINT",FACE,{"disambiguationData":[TD([[makeQuery(id+"F1.imprint","IMPRINT",EDGE,{"derivedFrom":subQ0}),1.0]])]});}
            var Q27;
            {var subQ1=sQuery(id+"F1.wireOp",EDGE,"dK6GBwfm-dPqC-hjEa-iTYE-RVy4wlrFdkMM");Q27=makeQuery(id+"F1.imprint","IMPRINT",FACE,{"disambiguationData":[TD([[makeQuery(id+"F1.imprint","IMPRINT",EDGE,{"derivedFrom":subQ1}),-1.0]])]});}
            var Q28;
            Q28=makeQuery(id+"F1.imprint","IMPRINT",FACE,{"disambiguationData":[TD([[makeQuery(id+"F1.imprint","IMPRINT",EDGE,{"derivedFrom":sQuery(id+"F1.wireOp",EDGE,"oubymV8D-XFeb-0PAk-4JDL-xSM2nJLgsDis.bottom")}),1.0]])]});
            var Q29;
            Q29=makeQuery(id+"F1.imprint","IMPRINT",FACE,{"disambiguationData":[TD([[makeQuery(id+"F1.imprint","IMPRINT",EDGE,{"derivedFrom":sQuery(id+"F1.wireOp",EDGE,"f12bf30a-3fb0-4a07-ab82-a452eb842c4a0.MirrorCS")}),1.0]])]});
            var Q30;
            Q30=makeQuery(id+"F1.imprint","IMPRINT",FACE,{"disambiguationData":[TD([[makeQuery(id+"F1.imprint","IMPRINT",EDGE,{"derivedFrom":sQuery(id+"F1.wireOp",EDGE,"x3bkE9ok-lBYa-WYL9-BGqZ-ToqHtp7qAzv1.bottom")}),-1.0]])]});
            var Q31;
            Q31=makeQuery(id+"F1.imprint","IMPRINT",FACE,{"disambiguationData":[TD([[makeQuery(id+"F1.imprint","IMPRINT",EDGE,{"derivedFrom":sQuery(id+"F1.wireOp",EDGE,"r6yQYByt-FrOl-2ls4-tRRX-qfS0saTtiFgI.bottom")}),-1.0]])]});
            var Q32;
            {var subQ1=sQuery(id+"F1.wireOp",EDGE,"f07af9aa-d931-4bbd-a6ef-468d94ab62715.MirrorCS");Q32=makeQuery(id+"F1.imprint","IMPRINT",FACE,{"disambiguationData":[TD([[makeQuery(id+"F1.imprint","IMPRINT",EDGE,{"derivedFrom":subQ1}),-1.0]])]});}
            var Q33;
            Q33=makeQuery(id+"F1.imprint","IMPRINT",FACE,{"disambiguationData":[TD([[makeQuery(id+"F1.imprint","IMPRINT",EDGE,{"derivedFrom":sQuery(id+"F1.wireOp",EDGE,"f07af9aa-d931-4bbd-a6ef-468d94ab62710.MirrorCS")}),-1.0]])]});
            var Q34;
            Q34=makeQuery(id+"F1.imprint","IMPRINT",FACE,{"disambiguationData":[TD([[makeQuery(id+"F1.imprint","IMPRINT",EDGE,{"derivedFrom":sQuery(id+"F1.wireOp",EDGE,"hZaFki4G-bcrQ-uzL6-g0YA-YevogViTWi07.bottom")}),-1.0]])]});
            var Q35;
            Q35=makeQuery(id+"F1.imprint","IMPRINT",FACE,{"disambiguationData":[TD([[makeQuery(id+"F1.imprint","IMPRINT",EDGE,{"derivedFrom":sQuery(id+"F1.wireOp",EDGE,"49cfc5f4-62bb-45af-9d23-c87fc13a81c10.MirrorCS")}),-1.0]])]});
            var Q36;
            Q36=makeQuery(id+"F1.imprint","IMPRINT",FACE,{"disambiguationData":[TD([[makeQuery(id+"F1.imprint","IMPRINT",EDGE,{"derivedFrom":sQuery(id+"F1.wireOp",EDGE,"I2OIgpRi-oHj4-qof5-e2zE-DI84iGOKbreY")}),-1.0]])]});
            var Q37;
            Q37=makeQuery(id+"F1.imprint","IMPRINT",FACE,{"disambiguationData":[TD([[makeQuery(id+"F1.imprint","IMPRINT",EDGE,{"derivedFrom":sQuery(id+"F1.wireOp",EDGE,"9u3zi5Ku-mPWA-KL16-uemJ-6pkS1S4TVdBg.bottom")}),1.0]])]});
            var Q38;
            Q38=makeQuery(id+"F1.imprint","IMPRINT",FACE,{"disambiguationData":[TD([[makeQuery(id+"F1.imprint","IMPRINT",EDGE,{"derivedFrom":sQuery(id+"F1.wireOp",EDGE,"Pm5OX93t-FbKm-RDH9-mpXl-K2NB97CrzknG.bottom")}),1.0]])]});
            var Q39;
            Q39=makeQuery(id+"F1.imprint","IMPRINT",FACE,{"disambiguationData":[TD([[makeQuery(id+"F1.imprint","IMPRINT",EDGE,{"derivedFrom":sQuery(id+"F1.wireOp",EDGE,"M246s0M4-v2vL-WYbt-WBYo-0TE9L7twK265.bottom")}),-1.0]])]});
            extrude(context, id + "F2", {"entities" : qUnion([Q0, Q1, Q2, Q3, Q4, Q5, Q6, Q7, Q8, Q9, Q10, Q11, Q12, Q13, Q14, Q15, Q16, Q17, Q18, Q19, Q20, Q21, Q22, Q23, Q24, Q25, Q26, Q27, Q28, Q29, Q30, Q31, Q32, Q33, Q34, Q35, Q36, Q37, Q38, Q39]), "depth" : (getVariable(context, 'ply34')) * mm});
        }
    });
